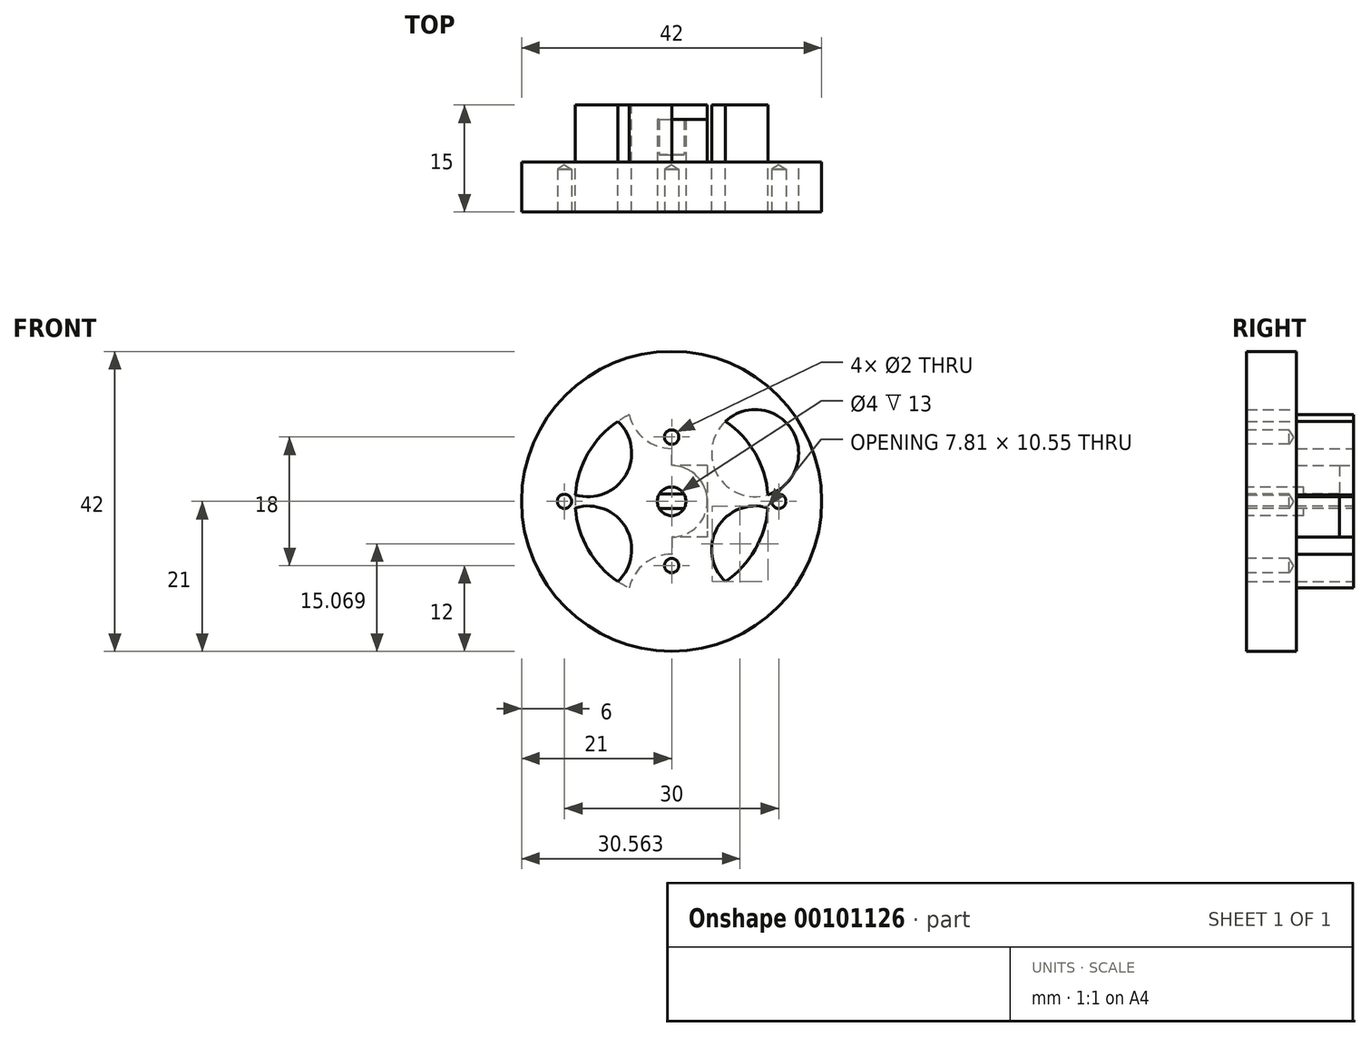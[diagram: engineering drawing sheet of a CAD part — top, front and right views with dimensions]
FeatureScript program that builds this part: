
annotation { "Feature Type Name" : "Feature", "Feature Type Description" : "" }
export const myFeature = defineFeature(function(context is Context, id is Id, definition is map)
    precondition{}
    {
        {
            var Q0;
            Q0=qCreatedBy(makeId("Front.planeOp"),FACE);
            var sketch = newSketch(context, id + "F0", { "sketchPlane" : qUnion([Q0])});
            skCircle(sketch, "E0", {"center": v(0, 0) * mm, "radius": 21 * mm});
            skCircle(sketch, "E1", {"center": v(0, 0) * mm, "radius": 13.5 * mm});
            skCircle(sketch, "E2", {"center": v(0, 13.5) * mm, "radius": 6.1 * mm});
            skLineSegment(sketch, "E3", {"start": v(0, 0) * mm, "end": v(0, 13.5) * mm});
            skLineSegment(sketch, "E4.3.0", {"start": v(0, 0) * mm, "end": v(0, -17.5) * mm});
            skCircle(sketch, "E5", {"center": v(0, 0) * mm, "radius": 5 * mm});
            skCircle(sketch, "E6.1.0", {"center": v(-11.7, 6.75) * mm, "radius": 6.1 * mm});
            skCircle(sketch, "E6.2.0", {"center": v(-11.7, -6.75) * mm, "radius": 6.1 * mm});
            skCircle(sketch, "E6.3.0", {"center": v(0, -13.5) * mm, "radius": 6.1 * mm});
            skCircle(sketch, "E6.4.0", {"center": v(11.7, -6.75) * mm, "radius": 6.1 * mm});
            skCircle(sketch, "E6.5.0", {"center": v(11.7, 6.75) * mm, "radius": 6.1 * mm});
            skSolve(sketch);
        }
        {
            var Q0;
            Q0 = qSketchRegion(id + "F0", true);
            var Q1;
            {var subQ3=sQuery(id+"F0.wireOp",EDGE,"tZOFWktZ-ElV9-8rvC-aUia-Pu95TyRWtfmy");var subQ5=sQuery(id+"F0.wireOp",EDGE,"E1");var subQ6=makeQuery(id+"F0.imprint","INTERSECT",VERTEX,{"disambiguationData":[OD(1.0)],"derivedFrom":[subQ5,subQ3]});Q1=makeQuery(id+"F0.imprint","IMPRINT",FACE,{"disambiguationData":[TD([[makeQuery(id+"F0.imprint","IMPRINT",EDGE,{"disambiguationData":[TD([[subQ6,-1.0]])],"derivedFrom":subQ5}),1.0]])]});}
            var Q2;
            {var subQ3=sQuery(id+"F0.wireOp",EDGE,"KCc62wJ9-mbiY-6kxt-bQFC-ecyapfwqHlXu");var subQ5=sQuery(id+"F0.wireOp",EDGE,"E1");var subQ6=makeQuery(id+"F0.imprint","INTERSECT",VERTEX,{"disambiguationData":[OD(1.0)],"derivedFrom":[subQ5,subQ3]});Q2=makeQuery(id+"F0.imprint","IMPRINT",FACE,{"disambiguationData":[TD([[makeQuery(id+"F0.imprint","IMPRINT",EDGE,{"disambiguationData":[TD([[subQ6,-1.0]])],"derivedFrom":subQ5}),1.0]])]});}
            var Q3;
            {var subQ3=sQuery(id+"F0.wireOp",EDGE,"0Yy4USeo-LOO3-cS4v-iVgx-1SsoAEMeRNpn");var subQ5=sQuery(id+"F0.wireOp",EDGE,"E1");var subQ6=makeQuery(id+"F0.imprint","INTERSECT",VERTEX,{"disambiguationData":[OD(1.0)],"derivedFrom":[subQ5,subQ3]});Q3=makeQuery(id+"F0.imprint","IMPRINT",FACE,{"disambiguationData":[TD([[makeQuery(id+"F0.imprint","IMPRINT",EDGE,{"disambiguationData":[TD([[subQ6,-1.0]])],"derivedFrom":subQ5}),1.0]])]});}
            var Q4;
            {var subQ5=sQuery(id+"F0.wireOp",EDGE,"E1");var subQ7=sQuery(id+"F0.wireOp",EDGE,"54YZh0VT-RaSH-f3J3-LX5H-yRfJ3TOlvn7D");var subQ8=makeQuery(id+"F0.imprint","INTERSECT",VERTEX,{"disambiguationData":[OD(0.0)],"derivedFrom":[subQ5,subQ7]});Q4=makeQuery(id+"F0.imprint","IMPRINT",FACE,{"disambiguationData":[TD([[makeQuery(id+"F0.imprint","IMPRINT",EDGE,{"disambiguationData":[TD([[subQ8,-1.0]])],"derivedFrom":subQ5}),1.0]])]});}
            var Q5;
            {var subQ3=sQuery(id+"F0.wireOp",EDGE,"E2");var subQ6=sQuery(id+"F0.wireOp",EDGE,"E1");var subQ9=makeQuery(id+"F0.imprint","INTERSECT",VERTEX,{"disambiguationData":[OD(1.0)],"derivedFrom":[subQ6,subQ3]});Q5=makeQuery(id+"F0.imprint","IMPRINT",FACE,{"disambiguationData":[TD([[makeQuery(id+"F0.imprint","IMPRINT",EDGE,{"disambiguationData":[TD([[subQ9,-1.0]])],"derivedFrom":subQ6}),1.0]])]});}
            var Q6;
            {var subQ0=sQuery(id+"F0.wireOp",EDGE,"E1");var subQ1=makeQuery(id+"F0.imprint","INTERSECT",VERTEX,{"derivedFrom":[subQ0,sQuery(id+"F0.wireOp",EDGE,"E4.3.0")]});Q6=makeQuery(id+"F0.imprint","IMPRINT",FACE,{"disambiguationData":[TD([[makeQuery(id+"F0.imprint","IMPRINT",EDGE,{"disambiguationData":[TD([[subQ1,1.0]])],"derivedFrom":subQ0}),-1.0]])]});}
            var Q7;
            {var subQ0=sQuery(id+"F0.wireOp",EDGE,"E4.3.0");var subQ1=sQuery(id+"F0.wireOp",EDGE,"E1");var subQ2=makeQuery(id+"F0.imprint","INTERSECT",VERTEX,{"derivedFrom":[subQ1,subQ0]});Q7=makeQuery(id+"F0.imprint","IMPRINT",FACE,{"disambiguationData":[TD([[makeQuery(id+"F0.imprint","IMPRINT",EDGE,{"disambiguationData":[TD([[subQ2,-1.0]])],"derivedFrom":subQ1}),1.0]])]});}
            var Q8;
            {var subQ0=sQuery(id+"F0.wireOp",EDGE,"E4.3.0");var subQ1=sQuery(id+"F0.wireOp",EDGE,"E1");var subQ2=makeQuery(id+"F0.imprint","INTERSECT",VERTEX,{"derivedFrom":[subQ1,subQ0]});Q8=makeQuery(id+"F0.imprint","IMPRINT",FACE,{"disambiguationData":[TD([[makeQuery(id+"F0.imprint","IMPRINT",EDGE,{"disambiguationData":[TD([[subQ2,1.0]])],"derivedFrom":subQ1}),1.0]])]});}
            var Q9;
            {var subQ0=sQuery(id+"F0.wireOp",EDGE,"E6.4.0");var subQ1=sQuery(id+"F0.wireOp",EDGE,"E1");var subQ2=makeQuery(id+"F0.imprint","INTERSECT",VERTEX,{"disambiguationData":[OD(0.0)],"derivedFrom":[subQ1,subQ0]});Q9=makeQuery(id+"F0.imprint","IMPRINT",FACE,{"disambiguationData":[TD([[makeQuery(id+"F0.imprint","IMPRINT",EDGE,{"disambiguationData":[TD([[subQ2,-1.0]])],"derivedFrom":subQ1}),-1.0]])]});}
            var Q10;
            {var subQ0=sQuery(id+"F0.wireOp",EDGE,"E6.5.0");var subQ1=sQuery(id+"F0.wireOp",EDGE,"E1");var subQ16=makeQuery(id+"F0.imprint","INTERSECT",VERTEX,{"disambiguationData":[OD(0.0)],"derivedFrom":[subQ1,subQ0]});Q10=makeQuery(id+"F0.imprint","IMPRINT",FACE,{"disambiguationData":[TD([[makeQuery(id+"F0.imprint","IMPRINT",EDGE,{"disambiguationData":[TD([[subQ16,-1.0]])],"derivedFrom":subQ1}),1.0]])]});}
            var Q11;
            {var subQ0=sQuery(id+"F0.wireOp",EDGE,"E4.3.0");var subQ1=sQuery(id+"F0.wireOp",EDGE,"E3");var subQ2=makeQuery(id+"F0.imprint","INTERSECT",VERTEX,{"derivedFrom":[subQ1,subQ0]});Q11=makeQuery(id+"F0.imprint","IMPRINT",FACE,{"disambiguationData":[TD([[makeQuery(id+"F0.imprint","IMPRINT",EDGE,{"disambiguationData":[TD([[subQ2,-1.0]])],"derivedFrom":subQ1}),-1.0]])]});}
            var Q12;
            {var subQ0=sQuery(id+"F0.wireOp",EDGE,"E4.3.0");var subQ1=sQuery(id+"F0.wireOp",EDGE,"E3");var subQ2=makeQuery(id+"F0.imprint","INTERSECT",VERTEX,{"derivedFrom":[subQ1,subQ0]});Q12=makeQuery(id+"F0.imprint","IMPRINT",FACE,{"disambiguationData":[TD([[makeQuery(id+"F0.imprint","IMPRINT",EDGE,{"disambiguationData":[TD([[subQ2,-1.0]])],"derivedFrom":subQ1}),1.0]])]});}
            var Q13;
            {var subQ0=sQuery(id+"F0.wireOp",EDGE,"E6.2.0");var subQ1=sQuery(id+"F0.wireOp",EDGE,"E1");var subQ2=makeQuery(id+"F0.imprint","INTERSECT",VERTEX,{"disambiguationData":[OD(0.0)],"derivedFrom":[subQ1,subQ0]});Q13=makeQuery(id+"F0.imprint","IMPRINT",FACE,{"disambiguationData":[TD([[makeQuery(id+"F0.imprint","IMPRINT",EDGE,{"disambiguationData":[TD([[subQ2,-1.0]])],"derivedFrom":subQ1}),-1.0]])]});}
            var Q14;
            {var subQ0=sQuery(id+"F0.wireOp",EDGE,"E6.1.0");var subQ1=sQuery(id+"F0.wireOp",EDGE,"E1");var subQ2=makeQuery(id+"F0.imprint","INTERSECT",VERTEX,{"disambiguationData":[OD(0.0)],"derivedFrom":[subQ1,subQ0]});Q14=makeQuery(id+"F0.imprint","IMPRINT",FACE,{"disambiguationData":[TD([[makeQuery(id+"F0.imprint","IMPRINT",EDGE,{"disambiguationData":[TD([[subQ2,-1.0]])],"derivedFrom":subQ1}),-1.0]])]});}
            var Q15;
            {var subQ0=sQuery(id+"F0.wireOp",EDGE,"E1");var subQ1=makeQuery(id+"F0.imprint","INTERSECT",VERTEX,{"derivedFrom":[subQ0,sQuery(id+"F0.wireOp",EDGE,"E3")]});Q15=makeQuery(id+"F0.imprint","IMPRINT",FACE,{"disambiguationData":[TD([[makeQuery(id+"F0.imprint","IMPRINT",EDGE,{"disambiguationData":[TD([[subQ1,1.0]])],"derivedFrom":subQ0}),-1.0]])]});}
            var Q16;
            {var subQ0=sQuery(id+"F0.wireOp",EDGE,"E3");var subQ1=sQuery(id+"F0.wireOp",EDGE,"E1");var subQ2=makeQuery(id+"F0.imprint","INTERSECT",VERTEX,{"derivedFrom":[subQ1,subQ0]});Q16=makeQuery(id+"F0.imprint","IMPRINT",FACE,{"disambiguationData":[TD([[makeQuery(id+"F0.imprint","IMPRINT",EDGE,{"disambiguationData":[TD([[subQ2,-1.0]])],"derivedFrom":subQ1}),1.0]])]});}
            var Q17;
            {var subQ0=sQuery(id+"F0.wireOp",EDGE,"E3");var subQ1=sQuery(id+"F0.wireOp",EDGE,"E1");var subQ2=makeQuery(id+"F0.imprint","INTERSECT",VERTEX,{"derivedFrom":[subQ1,subQ0]});Q17=makeQuery(id+"F0.imprint","IMPRINT",FACE,{"disambiguationData":[TD([[makeQuery(id+"F0.imprint","IMPRINT",EDGE,{"disambiguationData":[TD([[subQ2,1.0]])],"derivedFrom":subQ1}),1.0]])]});}
            var Q18;
            {var subQ0=sQuery(id+"F0.wireOp",EDGE,"E6.5.0");var subQ1=sQuery(id+"F0.wireOp",EDGE,"E1");var subQ2=makeQuery(id+"F0.imprint","INTERSECT",VERTEX,{"disambiguationData":[OD(0.0)],"derivedFrom":[subQ1,subQ0]});Q18=makeQuery(id+"F0.imprint","IMPRINT",FACE,{"disambiguationData":[TD([[makeQuery(id+"F0.imprint","IMPRINT",EDGE,{"disambiguationData":[TD([[subQ2,1.0]])],"derivedFrom":subQ1}),1.0]])]});}
            var Q19;
            {var subQ0=sQuery(id+"F0.wireOp",EDGE,"E6.5.0");var subQ1=sQuery(id+"F0.wireOp",EDGE,"E1");var subQ2=makeQuery(id+"F0.imprint","INTERSECT",VERTEX,{"disambiguationData":[OD(0.0)],"derivedFrom":[subQ1,subQ0]});Q19=makeQuery(id+"F0.imprint","IMPRINT",FACE,{"disambiguationData":[TD([[makeQuery(id+"F0.imprint","IMPRINT",EDGE,{"disambiguationData":[TD([[subQ2,1.0]])],"derivedFrom":subQ1}),-1.0]])]});}
            extrude(context, id + "F1", {"entities" : qUnion([Q0, Q1, Q2, Q3, Q4, Q5, Q6, Q7, Q8, Q9, Q10, Q11, Q12, Q13, Q14, Q15, Q16, Q17, Q18, Q19]), "depth" : 15 * mm});
        }
        {
            var Q0;
            {var subQ0=sQuery(id+"F0.wireOp",EDGE,"E6.5.0");var subQ1=sQuery(id+"F0.wireOp",EDGE,"E1");var subQ2=makeQuery(id+"F0.imprint","INTERSECT",VERTEX,{"disambiguationData":[OD(0.0)],"derivedFrom":[subQ1,subQ0]});Q0=makeQuery(id+"F0.imprint","IMPRINT",FACE,{"disambiguationData":[TD([[makeQuery(id+"F0.imprint","IMPRINT",EDGE,{"disambiguationData":[TD([[subQ2,1.0]])],"derivedFrom":subQ1}),1.0]])]});}
            var Q1;
            {var subQ0=sQuery(id+"F0.wireOp",EDGE,"E6.5.0");var subQ1=sQuery(id+"F0.wireOp",EDGE,"E1");var subQ2=makeQuery(id+"F0.imprint","INTERSECT",VERTEX,{"disambiguationData":[OD(0.0)],"derivedFrom":[subQ1,subQ0]});Q1=makeQuery(id+"F0.imprint","IMPRINT",FACE,{"disambiguationData":[TD([[makeQuery(id+"F0.imprint","IMPRINT",EDGE,{"disambiguationData":[TD([[subQ2,1.0]])],"derivedFrom":subQ1}),-1.0]])]});}
            var Q2;
            {var subQ0=sQuery(id+"F0.wireOp",EDGE,"E6.4.0");var subQ1=sQuery(id+"F0.wireOp",EDGE,"E1");var subQ2=makeQuery(id+"F0.imprint","INTERSECT",VERTEX,{"disambiguationData":[OD(0.0)],"derivedFrom":[subQ1,subQ0]});Q2=makeQuery(id+"F0.imprint","IMPRINT",FACE,{"disambiguationData":[TD([[makeQuery(id+"F0.imprint","IMPRINT",EDGE,{"disambiguationData":[TD([[subQ2,-1.0]])],"derivedFrom":subQ1}),-1.0]])]});}
            var Q3;
            {var subQ0=sQuery(id+"F0.wireOp",EDGE,"E6.4.0");var subQ1=sQuery(id+"F0.wireOp",EDGE,"E1");var subQ2=makeQuery(id+"F0.imprint","INTERSECT",VERTEX,{"disambiguationData":[OD(0.0)],"derivedFrom":[subQ1,subQ0]});Q3=makeQuery(id+"F0.imprint","IMPRINT",FACE,{"disambiguationData":[TD([[makeQuery(id+"F0.imprint","IMPRINT",EDGE,{"disambiguationData":[TD([[subQ2,-1.0]])],"derivedFrom":subQ1}),1.0]])]});}
            var Q4;
            {var subQ0=sQuery(id+"F0.wireOp",EDGE,"E4.3.0");var subQ1=sQuery(id+"F0.wireOp",EDGE,"E1");var subQ2=makeQuery(id+"F0.imprint","INTERSECT",VERTEX,{"derivedFrom":[subQ1,subQ0]});Q4=makeQuery(id+"F0.imprint","IMPRINT",FACE,{"disambiguationData":[TD([[makeQuery(id+"F0.imprint","IMPRINT",EDGE,{"disambiguationData":[TD([[subQ2,-1.0]])],"derivedFrom":subQ1}),1.0]])]});}
            var Q5;
            {var subQ0=sQuery(id+"F0.wireOp",EDGE,"E1");var subQ1=makeQuery(id+"F0.imprint","INTERSECT",VERTEX,{"derivedFrom":[subQ0,sQuery(id+"F0.wireOp",EDGE,"E4.3.0")]});Q5=makeQuery(id+"F0.imprint","IMPRINT",FACE,{"disambiguationData":[TD([[makeQuery(id+"F0.imprint","IMPRINT",EDGE,{"disambiguationData":[TD([[subQ1,1.0]])],"derivedFrom":subQ0}),-1.0]])]});}
            var Q6;
            {var subQ0=sQuery(id+"F0.wireOp",EDGE,"E4.3.0");var subQ1=sQuery(id+"F0.wireOp",EDGE,"E1");var subQ2=makeQuery(id+"F0.imprint","INTERSECT",VERTEX,{"derivedFrom":[subQ1,subQ0]});Q6=makeQuery(id+"F0.imprint","IMPRINT",FACE,{"disambiguationData":[TD([[makeQuery(id+"F0.imprint","IMPRINT",EDGE,{"disambiguationData":[TD([[subQ2,1.0]])],"derivedFrom":subQ1}),1.0]])]});}
            var Q7;
            {var subQ0=sQuery(id+"F0.wireOp",EDGE,"E6.2.0");var subQ1=sQuery(id+"F0.wireOp",EDGE,"E1");var subQ2=makeQuery(id+"F0.imprint","INTERSECT",VERTEX,{"disambiguationData":[OD(0.0)],"derivedFrom":[subQ1,subQ0]});Q7=makeQuery(id+"F0.imprint","IMPRINT",FACE,{"disambiguationData":[TD([[makeQuery(id+"F0.imprint","IMPRINT",EDGE,{"disambiguationData":[TD([[subQ2,-1.0]])],"derivedFrom":subQ1}),1.0]])]});}
            var Q8;
            {var subQ0=sQuery(id+"F0.wireOp",EDGE,"E6.2.0");var subQ1=sQuery(id+"F0.wireOp",EDGE,"E1");var subQ2=makeQuery(id+"F0.imprint","INTERSECT",VERTEX,{"disambiguationData":[OD(0.0)],"derivedFrom":[subQ1,subQ0]});Q8=makeQuery(id+"F0.imprint","IMPRINT",FACE,{"disambiguationData":[TD([[makeQuery(id+"F0.imprint","IMPRINT",EDGE,{"disambiguationData":[TD([[subQ2,-1.0]])],"derivedFrom":subQ1}),-1.0]])]});}
            var Q9;
            {var subQ0=sQuery(id+"F0.wireOp",EDGE,"E6.1.0");var subQ1=sQuery(id+"F0.wireOp",EDGE,"E1");var subQ2=makeQuery(id+"F0.imprint","INTERSECT",VERTEX,{"disambiguationData":[OD(0.0)],"derivedFrom":[subQ1,subQ0]});Q9=makeQuery(id+"F0.imprint","IMPRINT",FACE,{"disambiguationData":[TD([[makeQuery(id+"F0.imprint","IMPRINT",EDGE,{"disambiguationData":[TD([[subQ2,-1.0]])],"derivedFrom":subQ1}),1.0]])]});}
            var Q10;
            {var subQ0=sQuery(id+"F0.wireOp",EDGE,"E6.1.0");var subQ1=sQuery(id+"F0.wireOp",EDGE,"E1");var subQ2=makeQuery(id+"F0.imprint","INTERSECT",VERTEX,{"disambiguationData":[OD(0.0)],"derivedFrom":[subQ1,subQ0]});Q10=makeQuery(id+"F0.imprint","IMPRINT",FACE,{"disambiguationData":[TD([[makeQuery(id+"F0.imprint","IMPRINT",EDGE,{"disambiguationData":[TD([[subQ2,-1.0]])],"derivedFrom":subQ1}),-1.0]])]});}
            var Q11;
            {var subQ0=sQuery(id+"F0.wireOp",EDGE,"E3");var subQ1=sQuery(id+"F0.wireOp",EDGE,"E1");var subQ2=makeQuery(id+"F0.imprint","INTERSECT",VERTEX,{"derivedFrom":[subQ1,subQ0]});Q11=makeQuery(id+"F0.imprint","IMPRINT",FACE,{"disambiguationData":[TD([[makeQuery(id+"F0.imprint","IMPRINT",EDGE,{"disambiguationData":[TD([[subQ2,-1.0]])],"derivedFrom":subQ1}),1.0]])]});}
            var Q12;
            {var subQ0=sQuery(id+"F0.wireOp",EDGE,"E3");var subQ1=sQuery(id+"F0.wireOp",EDGE,"E1");var subQ2=makeQuery(id+"F0.imprint","INTERSECT",VERTEX,{"derivedFrom":[subQ1,subQ0]});Q12=makeQuery(id+"F0.imprint","IMPRINT",FACE,{"disambiguationData":[TD([[makeQuery(id+"F0.imprint","IMPRINT",EDGE,{"disambiguationData":[TD([[subQ2,1.0]])],"derivedFrom":subQ1}),1.0]])]});}
            var Q13;
            {var subQ0=sQuery(id+"F0.wireOp",EDGE,"E1");var subQ1=makeQuery(id+"F0.imprint","INTERSECT",VERTEX,{"derivedFrom":[subQ0,sQuery(id+"F0.wireOp",EDGE,"E3")]});Q13=makeQuery(id+"F0.imprint","IMPRINT",FACE,{"disambiguationData":[TD([[makeQuery(id+"F0.imprint","IMPRINT",EDGE,{"disambiguationData":[TD([[subQ1,1.0]])],"derivedFrom":subQ0}),-1.0]])]});}
            extrude(context, id + "F2", {"entities" : qUnion([Q0, Q1, Q2, Q3, Q4, Q5, Q6, Q7, Q8, Q9, Q10, Q11, Q12, Q13]), "operationType" : NewBodyOperationType.REMOVE, "depth" : 8 * mm});
        }
        {
            var Q0;
            Q0=makeQuery(id+"F1.opExtrude","CAP_FACE",FACE,{"disambiguationData":[OSD([sQuery(id+"F0.wireOp",EDGE,"E0")])],"isStart":true});
            var sketch = newSketch(context, id + "F3", { "sketchPlane" : qUnion([Q0])});
            skLineSegment(sketch, "E7.bottom", {"start": v(-5, 5) * mm, "end": v(5, 5) * mm});
            skLineSegment(sketch, "E7.top", {"start": v(-5, -5) * mm, "end": v(5, -5) * mm});
            skLineSegment(sketch, "E7.left", {"start": v(-5, 5) * mm, "end": v(-5, -5) * mm});
            skLineSegment(sketch, "E7.right", {"start": v(5, 5) * mm, "end": v(5, -5) * mm});
            skPoint(sketch, "E7.middle", {"position": v(0, 0) * mm});
            skSolve(sketch);
        }
        {
            var Q0;
            Q0=makeQuery(id+"F1.opExtrude","CAP_FACE",FACE,{"disambiguationData":[OSD([sQuery(id+"F0.wireOp",EDGE,"E0")])],"isStart":false});
            var sketch = newSketch(context, id + "F4", { "sketchPlane" : qUnion([Q0])});
            skLineSegment(sketch, "E8", {"start": v(0, 0) * mm, "end": v(-15, 0) * mm});
            skCircle(sketch, "E9", {"center": v(-15, 0) * mm, "radius": 1.5 * mm});
            skCircle(sketch, "E10.1.0", {"center": v(0, -15) * mm, "radius": 1.5 * mm});
            skCircle(sketch, "E10.2.0", {"center": v(15, 0) * mm, "radius": 1.5 * mm});
            skCircle(sketch, "E10.3.0", {"center": v(0, 15) * mm, "radius": 1.5 * mm});
            skPoint(sketch, "E10.center", {"position": v(0, 0) * mm});
            skSolve(sketch);
        }
        {
            var Q0;
            Q0=makeQuery(id+"F4.imprint","IMPRINT",FACE,{"disambiguationData":[TD([[makeQuery(id+"F4.imprint","IMPRINT",EDGE,{"derivedFrom":sQuery(id+"F4.wireOp",EDGE,"E9")}),-1.0]])]});
            var sketch = newSketch(context, id + "F5", { "sketchPlane" : qUnion([Q0])});
            skPoint(sketch, "E11", {"position": v(0, -9) * mm});
            skPoint(sketch, "E12", {"position": v(0, 9) * mm});
            skSolve(sketch);
        }
        {
            var Q0;
            Q0=sQuery(id+"F4.wireOp",VERTEX,"E9.center");
            var Q1;
            Q1=sQuery(id+"F4.wireOp",VERTEX,"E10.2.0.center");
            var Q2;
            Q2=sQuery(id+"F5.wireOp",VERTEX,"E11");
            var Q3;
            Q3=sQuery(id+"F5.wireOp",VERTEX,"E12");
            var Q4;
            Q4=makeQuery(id+"F1.opExtrude","SWEPT_BODY",BODY,{"disambiguationData":[OSD([sQuery(id+"F0.wireOp",EDGE,"E0")])]});
            hole(context, id + "F6", {"style" : HoleStyle.SIMPLE, "endStyle" : HoleEndStyle.BLIND, "holeDiameter" : 2 * mm, "holeDepth" : 6 * mm, "locations" : qUnion([Q0, Q1, Q2, Q3]), "scope" : qUnion([Q4])});
        }
        {
            var Q0;
            Q0=makeQuery(id+"F4.imprint","IMPRINT",FACE,{"disambiguationData":[TD([[makeQuery(id+"F4.imprint","IMPRINT",EDGE,{"derivedFrom":sQuery(id+"F4.wireOp",EDGE,"E9")}),-1.0]])]});
            var sketch = newSketch(context, id + "F7", { "sketchPlane" : qUnion([Q0])});
            skCircle(sketch, "E13", {"center": v(-13.3, -133.26) * mm, "radius": 2.1 * mm});
            skLineSegment(sketch, "E14", {"start": v(-15.1, -132.16) * mm, "end": v(-11.52, -132.16) * mm});
            skLineSegment(sketch, "E15", {"start": v(-15.1, -134.36) * mm, "end": v(-11.52, -134.36) * mm});
            skCircle(sketch, "E16", {"center": v(0, 0) * mm, "radius": 2 * mm});
            skLineSegment(sketch, "E17", {"start": v(-1.73, 1) * mm, "end": v(1.73, 1) * mm});
            skLineSegment(sketch, "E18", {"start": v(-1.73, -1) * mm, "end": v(1.73, -1) * mm});
            skSolve(sketch);
        }
        {
            var Q0;
            {var subQ0=sQuery(id+"F7.wireOp",EDGE,"E17");Q0=makeQuery(id+"F7.imprint","IMPRINT",FACE,{"disambiguationData":[TD([[makeQuery(id+"F7.imprint","IMPRINT",EDGE,{"derivedFrom":subQ0}),-1.0]])]});}
            extrude(context, id + "F8", {"entities" : qUnion([Q0]), "operationType" : NewBodyOperationType.REMOVE, "oppositeDirection" : true, "depth" : 15 * mm});
        }
        {
            var Q0;
            {var subQ0=sQuery(id+"F7.wireOp",EDGE,"E18");Q0=makeQuery(id+"F7.imprint","IMPRINT",FACE,{"disambiguationData":[TD([[makeQuery(id+"F7.imprint","IMPRINT",EDGE,{"derivedFrom":subQ0}),-1.0]])]});}
            var Q1;
            {var subQ0=sQuery(id+"F7.wireOp",EDGE,"E17");Q1=makeQuery(id+"F7.imprint","IMPRINT",FACE,{"disambiguationData":[TD([[makeQuery(id+"F7.imprint","IMPRINT",EDGE,{"derivedFrom":subQ0}),1.0]])]});}
            extrude(context, id + "F9", {"entities" : qUnion([Q0, Q1]), "operationType" : NewBodyOperationType.REMOVE, "oppositeDirection" : true, "depth" : 10 * mm});
        }
        {
            var Q0;
            Q0=makeQuery(id+"F9.boolean.opBoolean","COPY",FACE,{"derivedFrom":makeQuery(id+"F9.opExtrude","CAP_FACE",FACE,{"disambiguationData":[OSD([sQuery(id+"F7.wireOp",EDGE,"E16"),sQuery(id+"F7.wireOp",EDGE,"E17")])],"isStart":false})});
            var Q1;
            Q1=makeQuery(id+"F9.boolean.opBoolean","COPY",FACE,{"derivedFrom":makeQuery(id+"F9.opExtrude","CAP_FACE",FACE,{"disambiguationData":[OSD([sQuery(id+"F7.wireOp",EDGE,"E16"),sQuery(id+"F7.wireOp",EDGE,"E18")])],"isStart":false})});
            extrude(context, id + "F10", {"entities" : qUnion([Q0, Q1]), "operationType" : NewBodyOperationType.ADD, "depth" : 2 * mm});
        }
        {
            var Q0;
            Q0=makeQuery(id+"F3.imprint","IMPRINT",FACE,{"disambiguationData":[TD([[makeQuery(id+"F3.imprint","IMPRINT",EDGE,{"derivedFrom":sQuery(id+"F3.wireOp",EDGE,"E7.bottom")}),-1.0]])]});
            extrude(context, id + "F11", {"entities" : qUnion([Q0]), "operationType" : NewBodyOperationType.ADD, "oppositeDirection" : true, "depth" : 2 * mm});
        }
    });
